# Revit family: Louver_Wind-Drvn-Rn_ECV-645-MD_All-Lite
name_source: partatom
category: Windows
revit_build: Autodesk Revit 2013 (Build: 20120221_2030(x64)
units: mm (PartAtom-declared; Revit-internal decimal feet)

## types (1)
- Louver_Wind-Drvn-Rn_ECV-645_All-Lite
    # of Blades = 15
    04 CSI = 08 91 00
    95 CSI = 10200
    Air Volume Delivered (cfm) = 9,250
    Assembly Code = B2010300
    Blade Spacing = 4 "
    Blades = Mill finish, 6063-T5 Extruded Aluminum
    Blades Height = 55.9 "
    Cut Sheet = http://www.alllite.com
    Default Sill Height = 36 "
    Frame = Mill finish, 6063-T5 Extruded Aluminum
    Free Area Velocity (fpm) = 1,250
    Free Area for 48”x48” Louver = 46.0%
    Height = 60 "
    Installation = http://www.alllite.com
    Manufacturer = All-Lite
    Maximum Size - Multiple Section = Unlimited
    Maximum Size - Single Section = 60" x 120" or 120" x 60"
    Minimum Size = 12" x 12"
    Model = ECV-645
    OmniClass Code = 23-60 11 17
    OmniClass Title = Exterior Louvers and Grilles
    Pressure Loss (in.wg.) = 0.15
    Product URL = http://www.alllite-louvers.com
    Rough Height = 0 "
    Rough Width = 0 "
    Screen = Aluminum
    Screen Height = 54.3 "
    Screen Width = 59 "
    Shim Thickness = 0.5 "
    SmartBIM Object Version = 3
    Specifications = http://www.alllite.com
    URL = http://www.alllite-louvers.com
    Wall Closure = By host
    Warranty = http://www.alllite-louvers.com
    Width = 60 "

## geometry (parser evidence)
native form markers: Blend x18, Sweep x6
no freeform markers — native parametric forms only
